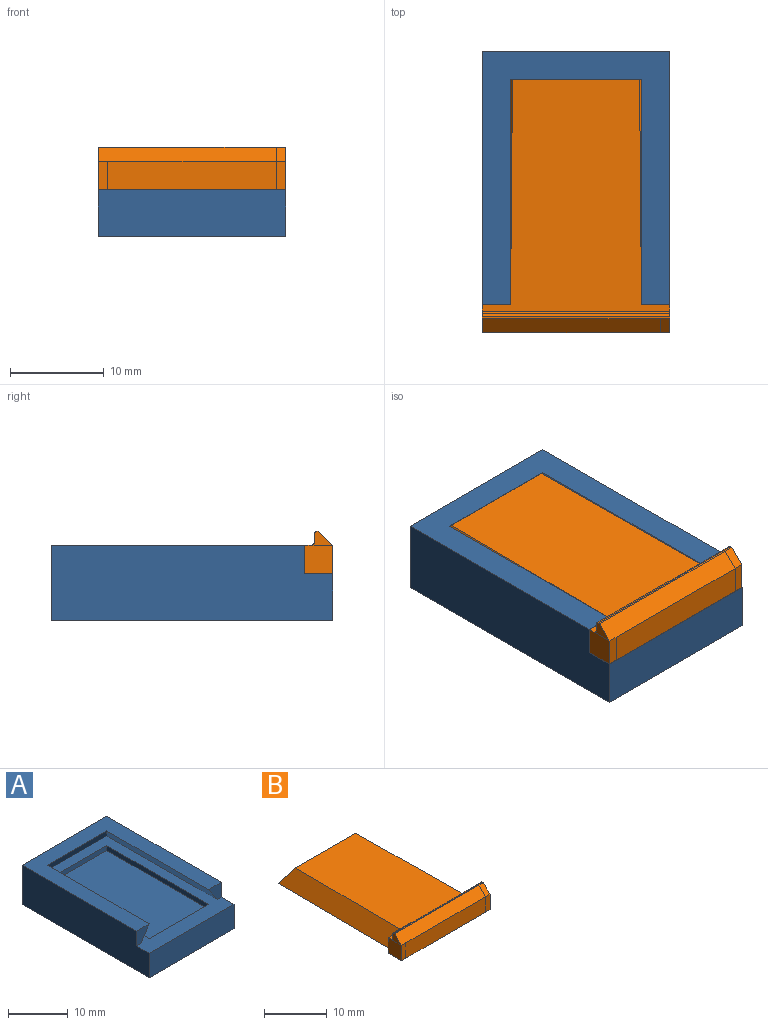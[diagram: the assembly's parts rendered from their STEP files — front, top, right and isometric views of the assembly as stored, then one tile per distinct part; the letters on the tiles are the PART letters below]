
ASSEMBLY  parts=2 mates=1
PART A: 17 faces, bbox 20x30x8 mm
  f0: plane 29x20mm, normal (0,0,1), area 192mm2, adj f1,f2,f4,f6,f7,f8,f9,f11
  f1: plane 20x5mm, normal (0,-1,0), area 100mm2, adj f0,f2,f4,f5
  f2: plane 30x8mm, normal (1,0,0), area 231mm2, adj f0,f1,f3,f5,f11,f13
  f3: plane 20x8mm, normal (0,1,0), area 160mm2, adj f2,f4,f5,f13
  f4: plane 30x8mm, normal (-1,0,0), area 231mm2, adj f0,f1,f3,f5,f12,f13
  f5: plane 30x20mm, normal (0,0,-1), area 600mm2, adj f1,f2,f3,f4
  f6: plane 14x1mm, normal (0,1,0), area 14mm2, adj f0,f7,f9,f10
  f7: plane 24x1mm, normal (-1,0,0), area 24mm2, adj f0,f6,f8,f10
  f8: plane 14x1mm, normal (0,-1,0), area 14mm2, adj f0,f7,f9,f10
  f9: plane 24x1mm, normal (1,0,0), area 24mm2, adj f0,f6,f8,f10
  f10: plane 24x14mm, normal (0,0,1), area 336mm2, adj f6,f7,f8,f9
  f11: plane 3x3mm, normal (0,-1,0), area 6mm2, adj f0,f2,f13,f16
  f12: plane 3x3mm, normal (0,-1,0), area 6mm2, adj f0,f4,f13,f14
  f13: plane 27x20mm, normal (0,0,1), area 204mm2, adj f2,f3,f4,f11,f12,f14,f15,f16
  f14: plane 26x3mm, normal (0.83,0,-0.55), area 90.1mm2, adj f0,f12,f13,f15
  f15: plane 18x3mm, normal (0,-0.83,-0.55), area 57.7mm2, adj f0,f13,f14,f16
  f16: plane 26x3mm, normal (-0.83,0,-0.55), area 90.1mm2, adj f0,f11,f13,f15
PART B: 19 faces, bbox 19.9x29x4.5 mm
  f0: plane 24.7x19.95mm, normal (0,0,1), area 343.7mm2, adj f1,f2,f6,f7,f9,f10,f11,f15
  f1: plane 3x3mm, normal (0,1,0), area 6mm2, adj f0,f2,f8,f11
  f2: plane 3x3mm, normal (-1,0,0), area 9mm2, adj f0,f1,f3,f8,f13
  f3: plane 3x1mm, normal (0,-1,0), area 3mm2, adj f2,f4,f8,f17
  f4: plane 17.95x3mm, normal (0,-1,0), area 53.8mm2, adj f3,f5,f8,f17
  f5: plane 3x1mm, normal (0,-1,0), area 3mm2, adj f4,f6,f8,f18
  f6: plane 4.5x3mm, normal (1,0,0), area 10.9mm2, adj f0,f5,f7,f8,f12,f14,f15,f16
  f7: plane 3x3mm, normal (0,1,0), area 6mm2, adj f0,f6,f8,f9
  f8: plane 29x19.95mm, normal (0,0,-1), area 520.7mm2, adj f1,f2,f3,f4,f5,f6,f7,f9
  f9: plane 26x3mm, normal (0.83,0.01,0.55), area 90.1mm2, adj f0,f7,f8,f10
  f10: plane 17.5x3mm, normal (0,0.83,0.55), area 55.9mm2, adj f0,f8,f9,f11
  f11: plane 26x3mm, normal (-0.83,0.01,0.55), area 90.1mm2, adj f0,f1,f8,f10
  f12: plane 19.95x0.9mm, normal (0,1,0), area 18mm2, adj f6,f13,f15,f16
  f13: plane 2.3x1.5mm, normal (-1,0,0), area 1.9mm2, adj f2,f12,f14,f15,f16,f17
  f14: plane 19.95x0.2mm, normal (0,0,1), area 4mm2, adj f6,f13,f16,f17,f18
  f15: cylinder r=0.3mm len=19.95mm, axis (-1,0,0), area 9.4mm2, adj f0,f6,f12,f13
  f16: cylinder r=0.3mm len=19.95mm, axis (1,0,0), area 9.4mm2, adj f6,f12,f13,f14
  f17: plane 18.95x1.5mm, normal (0,-0.71,0.71), area 40.2mm2, adj f3,f4,f13,f14,f18
  f18: plane 1.5x1.5mm, normal (0,-0.71,0.71), area 2.1mm2, adj f5,f6,f14,f17
PLACE A at identity
PLACE B rot(axis=(0,0,-1),0deg) t=(160.46,-0.86,5)mm
MATE slider B.f4 <-> A.f1  axis (0,-1,0) through (0,-15,5)mm
